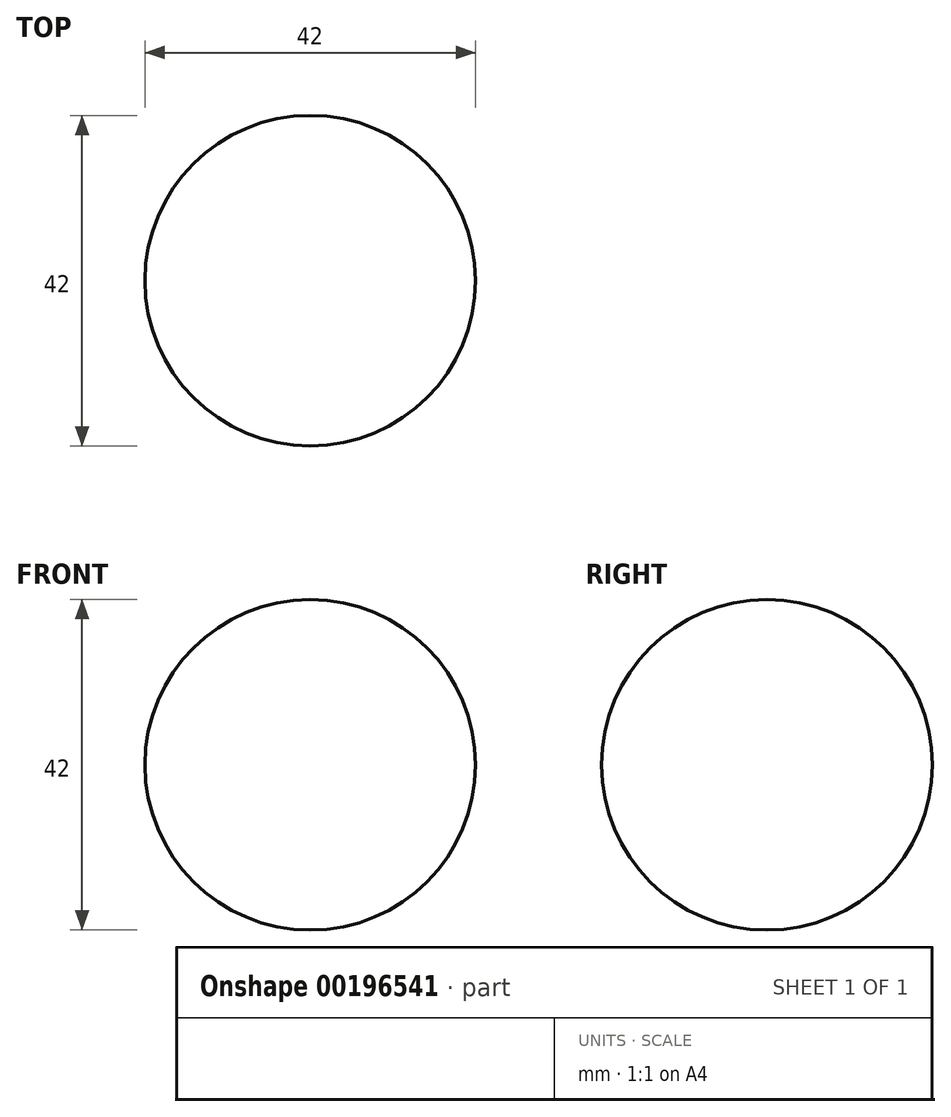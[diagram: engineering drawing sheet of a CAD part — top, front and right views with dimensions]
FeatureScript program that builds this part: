
annotation { "Feature Type Name" : "Feature", "Feature Type Description" : "" }
export const myFeature = defineFeature(function(context is Context, id is Id, definition is map)
    precondition{}
    {
        {
            var Q0;
            Q0=qCreatedBy(makeId("Front.planeOp"),FACE);
            var sketch = newSketch(context, id + "F0", { "sketchPlane" : qUnion([Q0])});
            skArc(sketch, "E0", {"start": v(0, 21) * mm, "mid": v(-21, 0) * mm, "end": v(0, -21) * mm});
            skLineSegment(sketch, "E1", {"start": v(0, 21) * mm, "end": v(0, -21) * mm});
            skSolve(sketch);
        }
        {
            var Q0;
            Q0=makeQuery(id+"F0.imprint","IMPRINT",FACE,{"disambiguationData":[TD([[makeQuery(id+"F0.imprint","IMPRINT",EDGE,{"derivedFrom":sQuery(id+"F0.wireOp",EDGE,"E0")}),1.0]])]});
            var Q1;
            Q1=sQuery(id+"F0.wireOp",EDGE,"E1");
            revolve(context, id + "F1", {"entities" : qUnion([Q0]), "axis" : qUnion([Q1]), "revolveType" : RevolveType.FULL});
        }
    });
